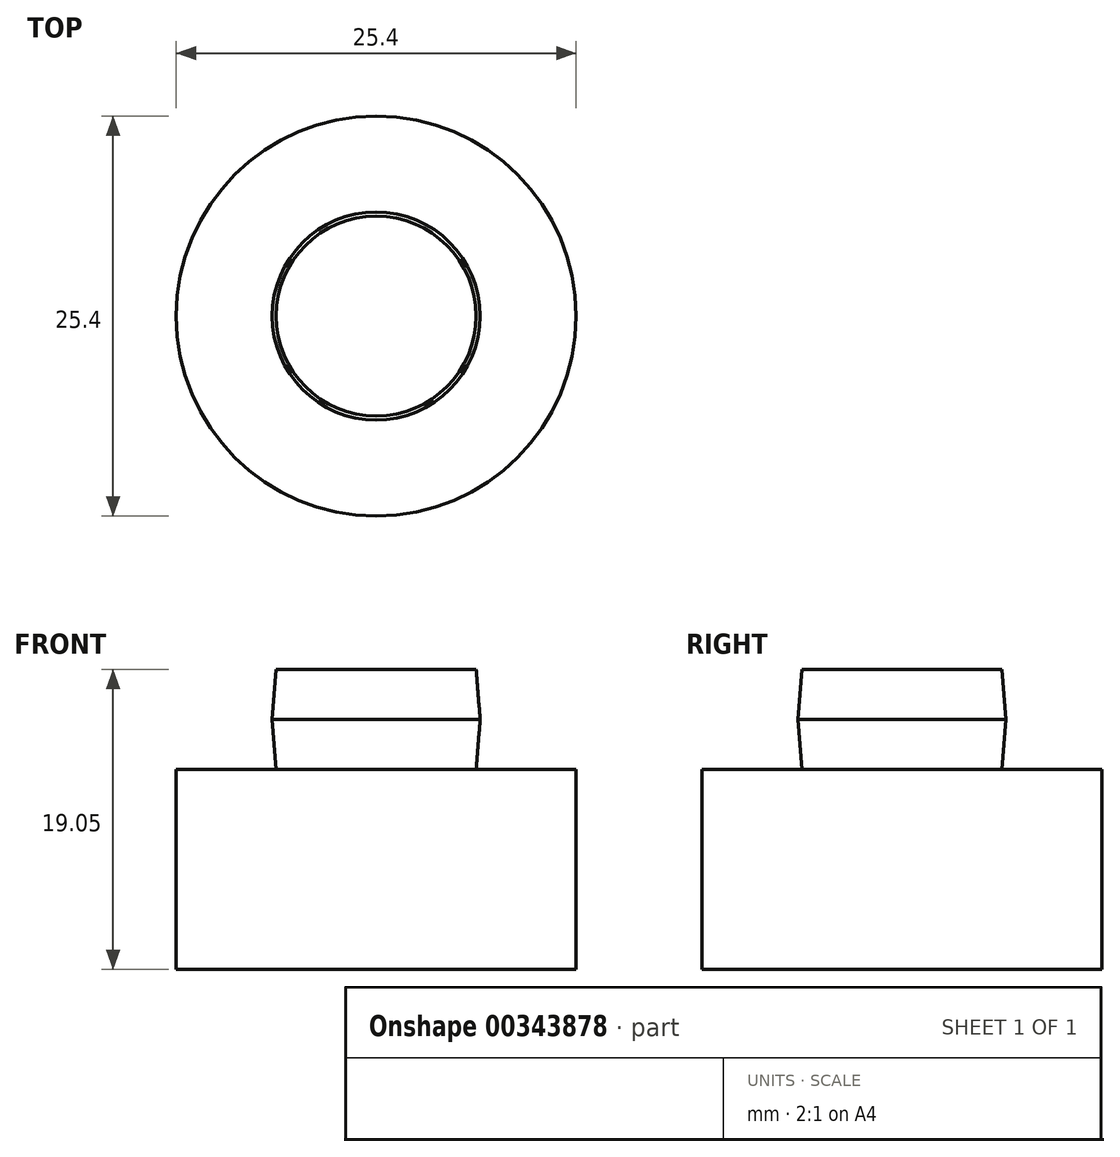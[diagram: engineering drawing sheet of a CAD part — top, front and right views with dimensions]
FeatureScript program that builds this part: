
annotation { "Feature Type Name" : "Feature", "Feature Type Description" : "" }
export const myFeature = defineFeature(function(context is Context, id is Id, definition is map)
    precondition{}
    {
        {
            var Q0;
            Q0=qCreatedBy(makeId("Front.planeOp"),FACE);
            var sketch = newSketch(context, id + "F0", { "sketchPlane" : qUnion([Q0])});
            skLineSegment(sketch, "E0", {"start": v(0, 0) * mm, "end": v(-12.7, 0) * mm});
            skLineSegment(sketch, "E1", {"start": v(-12.7, 0) * mm, "end": v(-12.7, 12.7) * mm});
            skLineSegment(sketch, "E2", {"start": v(-12.7, 12.7) * mm, "end": v(-6.35, 12.7) * mm});
            skLineSegment(sketch, "E3", {"start": v(-6.35, 12.7) * mm, "end": v(-6.35, 19.05) * mm});
            skLineSegment(sketch, "E4", {"start": v(-6.35, 19.05) * mm, "end": v(0, 19.05) * mm});
            skLineSegment(sketch, "E5", {"start": v(0, 19.05) * mm, "end": v(0, 0) * mm});
            skLineSegment(sketch, "E6", {"start": v(-6.35, 12.7) * mm, "end": v(-6.6, 15.88) * mm});
            skLineSegment(sketch, "E7", {"start": v(-6.6, 15.88) * mm, "end": v(-6.35, 19.05) * mm});
            skSolve(sketch);
        }
        {
            var Q0;
            Q0=makeQuery(id+"F0.imprint","IMPRINT",FACE,{"disambiguationData":[TD([[makeQuery(id+"F0.imprint","IMPRINT",EDGE,{"derivedFrom":sQuery(id+"F0.wireOp",EDGE,"E3")}),1.0]])]});
            var Q1;
            Q1=makeQuery(id+"F0.imprint","IMPRINT",FACE,{"disambiguationData":[TD([[makeQuery(id+"F0.imprint","IMPRINT",EDGE,{"derivedFrom":sQuery(id+"F0.wireOp",EDGE,"E0")}),-1.0]])]});
            var Q2;
            Q2=sQuery(id+"F0.wireOp",EDGE,"E5");
            revolve(context, id + "F1", {"entities" : qUnion([Q0, Q1]), "axis" : qUnion([Q2]), "revolveType" : RevolveType.FULL});
        }
    });
